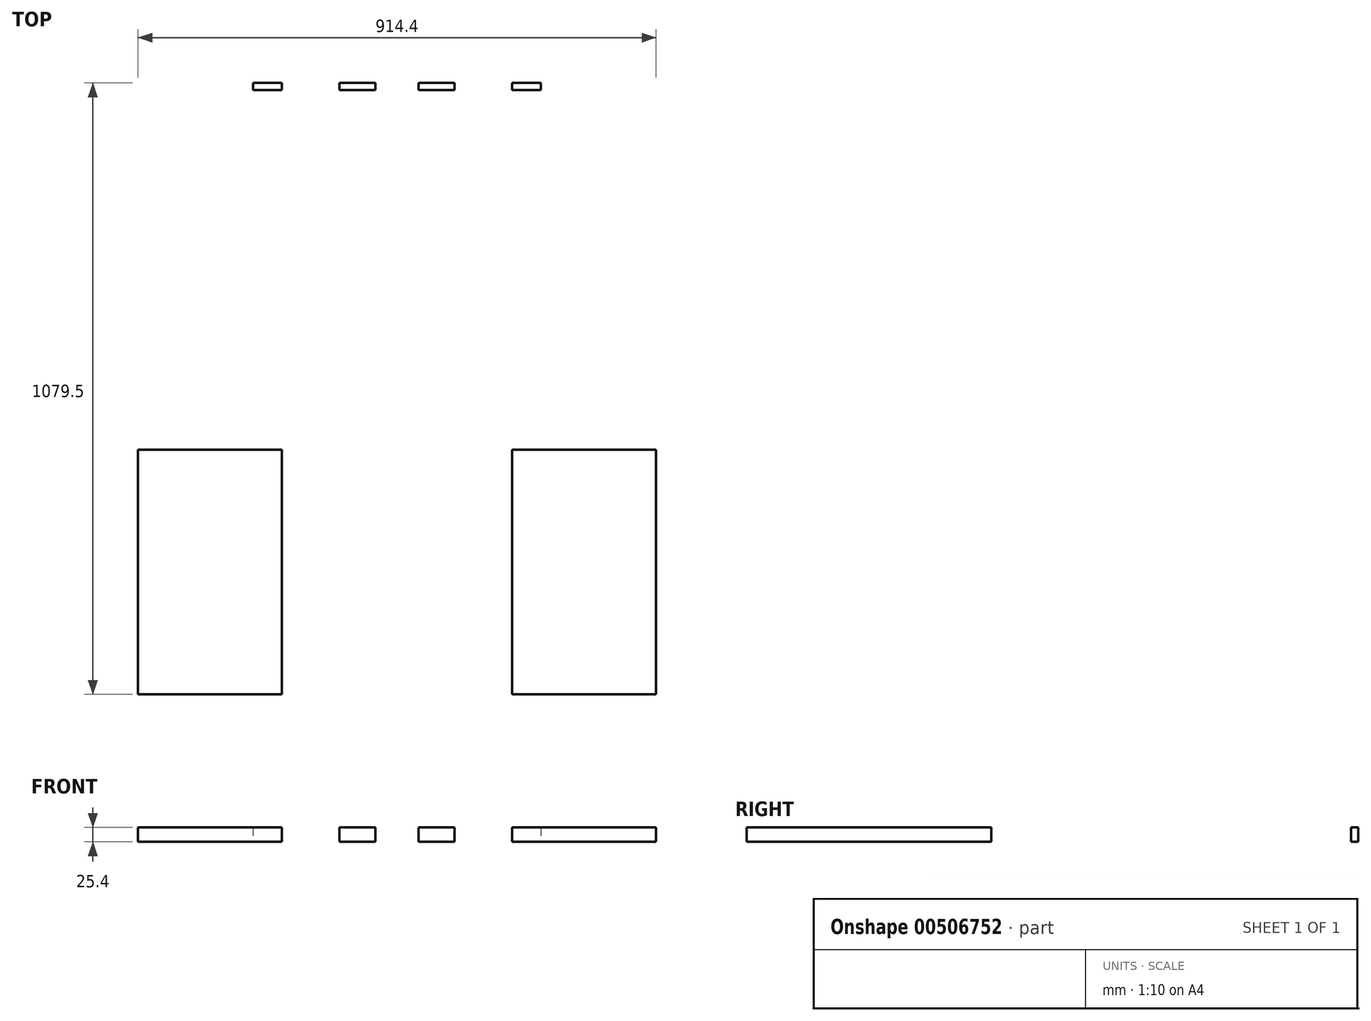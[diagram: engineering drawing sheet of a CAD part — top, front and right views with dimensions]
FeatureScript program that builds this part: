
annotation { "Feature Type Name" : "Feature", "Feature Type Description" : "" }
export const myFeature = defineFeature(function(context is Context, id is Id, definition is map)
    precondition{}
    {
        {
            var Q0;
            Q0=qCreatedBy(makeId("Top.planeOp"),FACE);
            var sketch = newSketch(context, id + "F0", { "sketchPlane" : qUnion([Q0])});
            skLineSegment(sketch, "E0.top", {"start": v(-660.4, -1396.32) * mm, "end": v(254, -1396.32) * mm});
            skLineSegment(sketch, "E0.left", {"start": v(-660.4, -454.31) * mm, "end": v(-660.4, -1396.32) * mm});
            skLineSegment(sketch, "E0.right", {"start": v(254, -454.31) * mm, "end": v(254, -1396.32) * mm});
            skLineSegment(sketch, "E1", {"start": v(-660.4, -454.31) * mm, "end": v(-406.4, 127.68) * mm});
            skLineSegment(sketch, "E2", {"start": v(-406.4, 127.68) * mm, "end": v(0, 127.68) * mm});
            skLineSegment(sketch, "E3", {"start": v(0, 127.68) * mm, "end": v(254, -454.31) * mm});
            skLineSegment(sketch, "E4.bottom", {"start": v(-241.3, 76.88) * mm, "end": v(-165.1, 76.88) * mm});
            skLineSegment(sketch, "E4.top", {"start": v(-241.3, -354.92) * mm, "end": v(-165.1, -354.92) * mm});
            skLineSegment(sketch, "E4.left", {"start": v(-241.3, 76.88) * mm, "end": v(-241.3, -354.92) * mm});
            skLineSegment(sketch, "E4.right", {"start": v(-165.1, 76.88) * mm, "end": v(-165.1, -354.92) * mm});
            skLineSegment(sketch, "E5.bottom", {"start": v(-660.4, -964.52) * mm, "end": v(-406.4, -964.52) * mm});
            skLineSegment(sketch, "E5.top", {"start": v(-660.4, -1396.32) * mm, "end": v(-406.4, -1396.32) * mm});
            skLineSegment(sketch, "E5.left", {"start": v(-660.4, -964.52) * mm, "end": v(-660.4, -1396.32) * mm});
            skLineSegment(sketch, "E5.right", {"start": v(-406.4, -964.52) * mm, "end": v(-406.4, -1396.32) * mm});
            skLineSegment(sketch, "E6.bottom", {"start": v(0, -964.52) * mm, "end": v(254, -964.52) * mm});
            skLineSegment(sketch, "E6.top", {"start": v(0, -1396.32) * mm, "end": v(254, -1396.32) * mm});
            skLineSegment(sketch, "E6.left", {"start": v(254, -964.52) * mm, "end": v(254, -1396.32) * mm});
            skLineSegment(sketch, "E6.right", {"start": v(0, -964.52) * mm, "end": v(0, -1396.32) * mm});
            skPoint(sketch, "E7.firstSnap0", {"position": v(-203.2, -354.92) * mm});
            skLineSegment(sketch, "E8.bottom", {"start": v(50.8, -329.52) * mm, "end": v(-457.2, -329.52) * mm});
            skLineSegment(sketch, "E8.top", {"start": v(50.8, -316.82) * mm, "end": v(-457.2, -316.82) * mm});
            skLineSegment(sketch, "E8.left", {"start": v(50.8, -329.52) * mm, "end": v(50.8, -316.82) * mm});
            skLineSegment(sketch, "E8.right", {"start": v(-457.2, -329.52) * mm, "end": v(-457.2, -316.82) * mm});
            skLineSegment(sketch, "E9", {"start": v(0, -316.82) * mm, "end": v(0, -329.52) * mm});
            skLineSegment(sketch, "E10", {"start": v(-101.6, -316.82) * mm, "end": v(-101.6, -329.52) * mm});
            skLineSegment(sketch, "E11", {"start": v(-304.8, -316.82) * mm, "end": v(-304.8, -329.52) * mm});
            skLineSegment(sketch, "E12", {"start": v(-406.4, -316.82) * mm, "end": v(-406.4, -329.52) * mm});
            skCircle(sketch, "E13", {"center": v(-203.2, -714.33) * mm, "radius": 12.7 * mm});
            skSolve(sketch);
        }
        {
            var Q0;
            Q0=makeQuery(id+"F0.imprint","IMPRINT",FACE,{"disambiguationData":[TD([[makeQuery(id+"F0.imprint","IMPRINT",EDGE,{"derivedFrom":sQuery(id+"F0.wireOp",EDGE,"E0.top")}),1.0]])]});
            var Q1;
            {var subQ0=sQuery(id+"F0.wireOp",EDGE,"E8.right");Q1=makeQuery(id+"F0.imprint","IMPRINT",FACE,{"disambiguationData":[TD([[makeQuery(id+"F0.imprint","IMPRINT",EDGE,{"derivedFrom":subQ0}),-1.0]])]});}
            var Q2;
            {var subQ0=sQuery(id+"F0.wireOp",EDGE,"KvvOJgAv-tRtH-8fgD-CERq-NVAx6zXHpKqu");Q2=makeQuery(id+"F0.imprint","IMPRINT",FACE,{"disambiguationData":[TD([[makeQuery(id+"F0.imprint","IMPRINT",EDGE,{"derivedFrom":subQ0}),-1.0]])]});}
            var Q3;
            {var subQ0=sQuery(id+"F0.wireOp",EDGE,"E10");Q3=makeQuery(id+"F0.imprint","IMPRINT",FACE,{"disambiguationData":[TD([[makeQuery(id+"F0.imprint","IMPRINT",EDGE,{"derivedFrom":subQ0}),-1.0]])]});}
            var Q4;
            {var subQ0=sQuery(id+"F0.wireOp",EDGE,"E8.left");Q4=makeQuery(id+"F0.imprint","IMPRINT",FACE,{"disambiguationData":[TD([[makeQuery(id+"F0.imprint","IMPRINT",EDGE,{"derivedFrom":subQ0}),1.0]])]});}
            var Q5;
            {var subQ5=sQuery(id+"F0.wireOp",EDGE,"E11");Q5=makeQuery(id+"F0.imprint","IMPRINT",FACE,{"disambiguationData":[TD([[makeQuery(id+"F0.imprint","IMPRINT",EDGE,{"derivedFrom":subQ5}),1.0]])]});}
            extrude(context, id + "F1", {"entities" : qUnion([Q0, Q1, Q2, Q3, Q4, Q5]), "depth" : 25.4 * mm, "offsetDistance" : 25.4 * mm});
        }
    });
